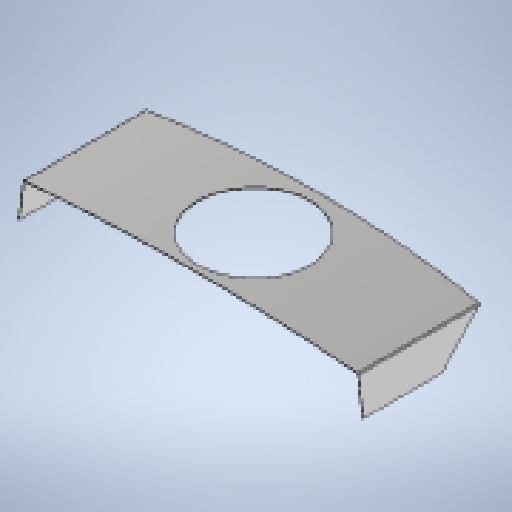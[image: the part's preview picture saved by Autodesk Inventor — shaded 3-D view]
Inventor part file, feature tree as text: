
AUTODESK INVENTOR PART (.ipt)
format: ipt  version: 2025.1 (Build 291241020, 241B)  size: 548,864 bytes
history: native  units: mm
features: projected_geometry x23, sheet_metal_op x5, sketch x3, other x3, extrude x1
ambient origin geometry x8: Origin, YZ Plane, XZ Plane, XY Plane, X Axis, Y Axis, Z Axis, Center Point
bodies: Solid1 (feature_tree)
feature tree (35):
  sheet_metal_op  "Contour Flange1"
  extrude  "Extrusion2"  Depth=32.0mm
  sheet_metal_op  "Unfold2"
  sheet_metal_op  "Refold2"
  sketch  "Sketch1"  dims[d0=1570.0mm d1=32.0mm]
  other  "Plate1"
  sheet_metal_op  "Bend1"
  sheet_metal_op  "Corner1"
  sketch  "Sketch3"  dims[d2=40.0mm]
  sketch  "Sketch7"  dims[d3=3.0mm d4=3.0mm d5=1.5mm d6=6.0mm d7=3.0mm d8=580.0mm d9=3.0mm d10=0.5mm d11=12.0mm d12=3.0mm d13=3.0mm d14=3.0mm d15=160.0mm d16=17.008234mm d21=8688.265625mm d22=500.0mm d23=3.0mm d24=0.0mm d25=300.0mm d39=350.0mm d41=3.0mm d42=0.0mm d43=545.0mm]
  projected_geometry  "Projected Loop7"
  projected_geometry  "Projected Loop8"
  projected_geometry  "Projected Loop9"
  projected_geometry  "Projected Loop10"
  projected_geometry  "Projected Loop11"
  projected_geometry  "Projected Loop12"
  projected_geometry  "Projected Loop13"
  projected_geometry  "Projected Loop14"
  projected_geometry  "Projected Loop15"
  projected_geometry  "Projected Loop16"
  projected_geometry  "Projected Loop17"
  projected_geometry  "Projected Loop18"
  projected_geometry  "Projected Loop19"
  projected_geometry  "Projected Loop20"
  projected_geometry  "Projected Loop21"
  projected_geometry  "Projected Loop22"
  projected_geometry  "Projected Loop23"
  projected_geometry  "Projected Loop24"
  projected_geometry  "Projected Loop25"
  projected_geometry  "Projected Loop26"
  projected_geometry  "Projected Loop27"
  projected_geometry  "Projected Loop28"
  projected_geometry  "Projected Loop29"
  other  "Cut1"
  other  "Definition1"
